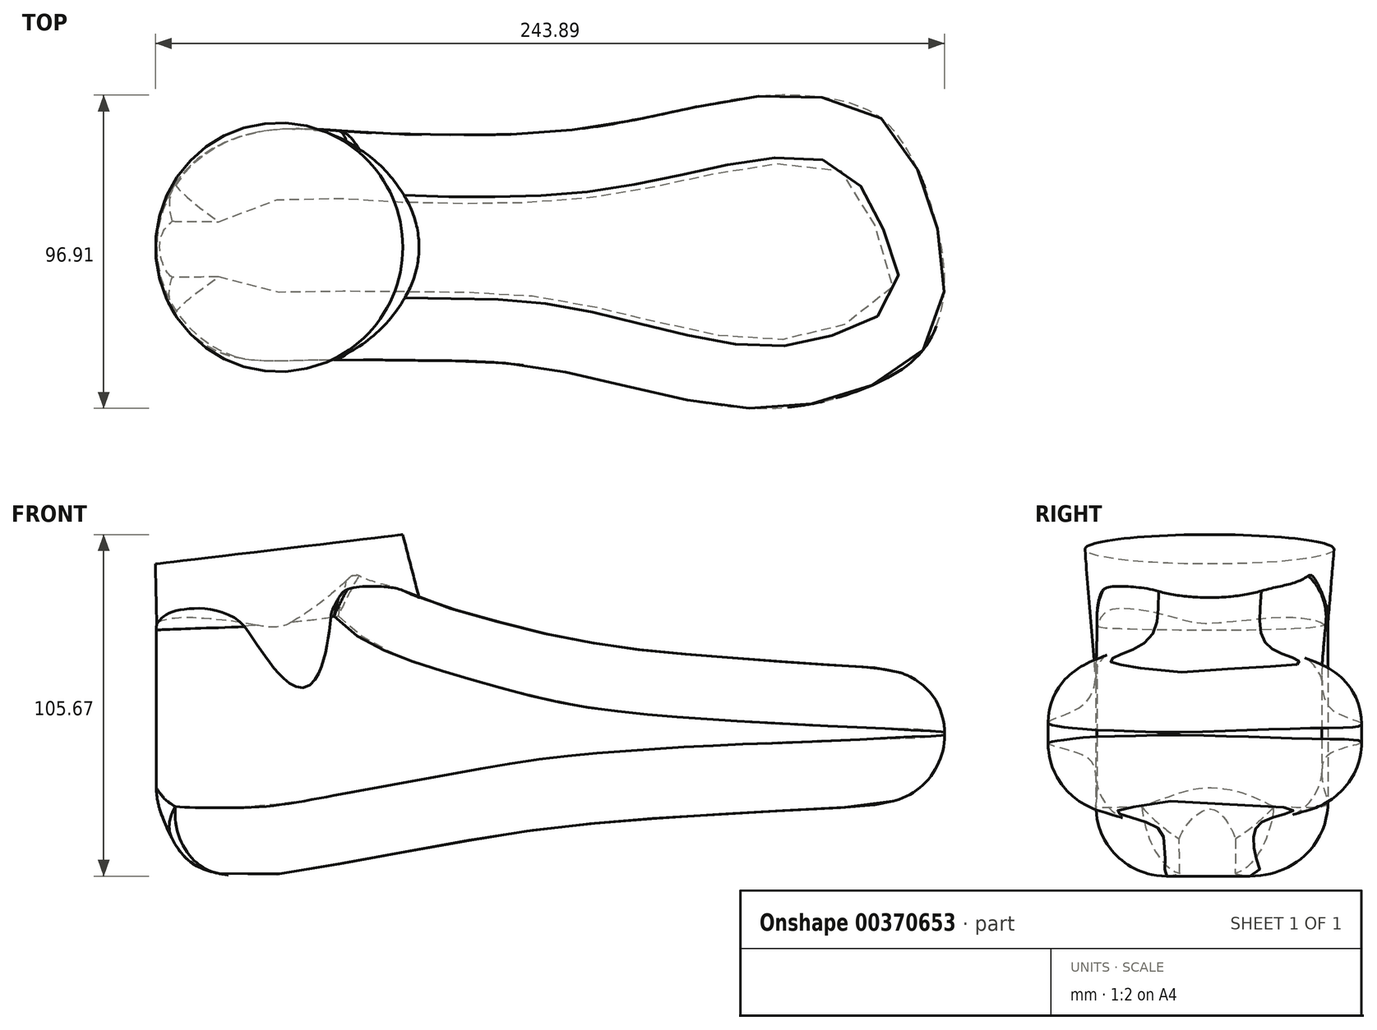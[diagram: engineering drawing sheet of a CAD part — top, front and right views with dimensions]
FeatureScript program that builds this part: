
annotation { "Feature Type Name" : "Feature", "Feature Type Description" : "" }
export const myFeature = defineFeature(function(context is Context, id is Id, definition is map)
    precondition{}
    {
        {
            var Q0;
            Q0=qCreatedBy(makeId("Top.planeOp"),FACE);
            cPlane(context, id + "F0", {"entities" : qUnion([Q0]), "cplaneType" : CPlaneType.OFFSET, "offset" : 10 * mm, "oppositeDirection" : true, "width" : 150 * mm, "height" : 150 * mm});
        }
        {
            var Q0;
            Q0=qCreatedBy(makeId("Front.planeOp"),FACE);
            var sketch = newSketch(context, id + "F1", { "sketchPlane" : qUnion([Q0])});
            skLineSegment(sketch, "E0", {"start": v(-126.2, 34.59) * mm, "end": v(0, 49.64) * mm, "construction": true});
            skSolve(sketch);
        }
        {
            var Q0;
            Q0=qCreatedBy(makeId("Right.planeOp"),FACE);
            var sketch = newSketch(context, id + "F2", { "sketchPlane" : qUnion([Q0])});
            skLineSegment(sketch, "E1.0", {"start": v(0, 34.59) * mm, "end": v(0, 49.64) * mm, "construction": true});
            skLineSegment(sketch, "E2", {"start": v(0, 49.64) * mm, "end": v(78.18, 49.64) * mm, "construction": true});
            skSolve(sketch);
        }
        {
            var Q0;
            Q0=sQuery(id+"F2.wireOp",VERTEX,"E2.end");
            var Q1;
            Q1=sQuery(id+"F2.wireOp",VERTEX,"E2.start");
            var Q2;
            Q2=sQuery(id+"F1.wireOp",VERTEX,"E0.start");
            cPlane(context, id + "F3", {"entities" : qUnion([Q0, Q1, Q2]), "cplaneType" : CPlaneType.THREE_POINT, "offset" : 25 * mm, "width" : 150 * mm, "height" : 150 * mm});
        }
        {
            var Q0;
            Q0=qCreatedBy(id+"F0.planeOp",FACE);
            cPlane(context, id + "F4", {"entities" : qUnion([Q0]), "cplaneType" : CPlaneType.OFFSET, "offset" : 70 * mm, "width" : 150 * mm, "height" : 150 * mm});
        }
        {
            var Q0;
            Q0=qCreatedBy(id+"F4.planeOp",FACE);
            var sketch = newSketch(context, id + "F5", { "sketchPlane" : qUnion([Q0])});
            skLineSegment(sketch, "E3.bottom", {"start": v(178, 87.04) * mm, "end": v(-168.77, 87.04) * mm});
            skLineSegment(sketch, "E3.top", {"start": v(178, -71.84) * mm, "end": v(-168.77, -71.84) * mm});
            skLineSegment(sketch, "E3.left", {"start": v(178, 87.04) * mm, "end": v(178, -71.84) * mm});
            skLineSegment(sketch, "E3.right", {"start": v(-168.77, 87.04) * mm, "end": v(-168.77, -71.84) * mm});
            skFitSpline(sketch, "E4", {"points": [v(112.25, -42.37) * mm, v(125.46, -31.4) * mm, v(130.92, -15.26) * mm, v(129.4, 3.7) * mm, v(122.2, 25.52) * mm, v(108.35, 43.13) * mm, v(82.74, 48.96) * mm, v(59.98, 47) * mm, v(19.69, 38.96) * mm, v(-18.8, 36.21) * mm, v(-55.07, 36.97) * mm, v(-78, 38.15) * mm, v(-97.37, 35.08) * mm, v(-113.72, 24.15) * mm, v(-122.11, 6.16) * mm, v(-120.89, -12.02) * mm, v(-115.3, -23.54) * mm, v(-105.57, -32.28) * mm, v(-91.66, -36.26) * mm, v(-71.4, -36.26) * mm, v(-39.4, -36.46) * mm, v(-2.44, -38.24) * mm, v(40.03, -47.42) * mm, v(79.93, -51.64) * mm, v(112.25, -42.37) * mm]});
            skSolve(sketch);
        }
        {
            var Q0;
            Q0=qCreatedBy(makeId("Front.planeOp"),FACE);
            var sketch = newSketch(context, id + "F6", { "sketchPlane" : qUnion([Q0])});
            skFitSpline(sketch, "E5", {"points": [v(-119.13, 38.44) * mm, v(-119.13, 33.94) * mm, v(-120.9, 4.27) * mm, v(-123.57, -25.48) * mm, v(-120.92, -39.45) * mm, v(-113.66, -52.87) * mm, v(-104.36, -58.06) * mm, v(-92.75, -59.32) * mm, v(-77.53, -57.75) * mm, v(-27.63, -48.8) * mm, v(12.86, -42.84) * mm, v(69.82, -38.75) * mm, v(100.89, -37.03) * mm, v(116.9, -34.52) * mm, v(127.68, -28.43) * mm, v(131.34, -21.72) * mm, v(132.41, -11.5) * mm, v(130.12, -3.1) * mm, v(121.42, 4.53) * mm, v(108.1, 7.85) * mm, v(96.18, 8.64) * mm, v(56.48, 11.46) * mm, v(17.18, 15.9) * mm, v(-17.61, 23.97) * mm, v(-45.56, 34.04) * mm, v(-53.77, 42.25) * mm, v(-55.62, 46.48) * mm, v(-60.65, 45.69) * mm, v(-113.57, 39.24) * mm, v(-119.13, 38.44) * mm]});
            skSolve(sketch);
        }
        {
            var Q0;
            Q0 = qSketchRegion(id + "F6", true);
            extrude(context, id + "F7", {"entities" : qUnion([Q0]), "depth" : 140 * mm, "symmetric" : true});
        }
        {
            var Q0;
            Q0=makeQuery(id+"F5.imprint","IMPRINT",FACE,{"disambiguationData":[TD([[makeQuery(id+"F5.imprint","IMPRINT",EDGE,{"derivedFrom":sQuery(id+"F5.wireOp",EDGE,"E3.bottom")}),1.0]])]});
            extrude(context, id + "F8", {"entities" : qUnion([Q0]), "operationType" : NewBodyOperationType.REMOVE, "oppositeDirection" : true, "depth" : 130 * mm});
        }
        {
            var Q0;
            Q0=makeQuery(id+"F8.boolean.opBoolean","INTERSECT",EDGE,{"disambiguationData":[OD(1.0)],"derivedFrom":[makeQuery(id+"F7.opExtrude","SWEPT_FACE",FACE,{"disambiguationData":[OSD([sQuery(id+"F6.wireOp",EDGE,"E5")])]}),makeQuery(id+"F8.opExtrude","SWEPT_FACE",FACE,{"disambiguationData":[OSD([sQuery(id+"F5.wireOp",EDGE,"E4")])]})]});
            fillet(context, id + "F9", {"entities" : qUnion([Q0]), "radius" : 20 * mm, "allowEdgeOverflow" : false});
        }
        {
            var Q0;
            Q0=makeQuery(id+"F8.boolean.opBoolean","INTERSECT",EDGE,{"disambiguationData":[OD(0.0)],"derivedFrom":[makeQuery(id+"F7.opExtrude","SWEPT_FACE",FACE,{"disambiguationData":[OSD([sQuery(id+"F6.wireOp",EDGE,"E5")])]}),makeQuery(id+"F8.opExtrude","SWEPT_FACE",FACE,{"disambiguationData":[OSD([sQuery(id+"F5.wireOp",EDGE,"E4")])]})]});
            fillet(context, id + "F10", {"entities" : qUnion([Q0]), "radius" : 22 * mm, "tangentPropagation" : true, "allowEdgeOverflow" : false});
        }
        {
            var Q0;
            Q0=qCreatedBy(id+"F3.planeOp",FACE);
            var sketch = newSketch(context, id + "F11", { "sketchPlane" : qUnion([Q0])});
            skLineSegment(sketch, "E6.bottom", {"start": v(-167.37, -58.49) * mm, "end": v(31.87, -58.49) * mm});
            skLineSegment(sketch, "E6.top", {"start": v(-167.37, 81.96) * mm, "end": v(31.87, 81.96) * mm});
            skLineSegment(sketch, "E6.left", {"start": v(-167.37, -58.49) * mm, "end": v(-167.37, 81.96) * mm});
            skLineSegment(sketch, "E6.right", {"start": v(31.87, -58.49) * mm, "end": v(31.87, 81.96) * mm});
            skSolve(sketch);
        }
        {
            var Q0;
            Q0=makeQuery(id+"F11.imprint","IMPRINT",FACE,{"disambiguationData":[TD([[makeQuery(id+"F11.imprint","IMPRINT",EDGE,{"derivedFrom":sQuery(id+"F11.wireOp",EDGE,"E6.bottom")}),1.0]])]});
            extrude(context, id + "F12", {"entities" : qUnion([Q0]), "operationType" : NewBodyOperationType.REMOVE, "depth" : 10 * mm, "symmetric" : true});
        }
        {
            var Q0;
            Q0=makeQuery(id+"F7.opExtrude","SWEPT_BODY",BODY,{"disambiguationData":[OSD([sQuery(id+"F6.wireOp",EDGE,"E5")])]});
            var Q1;
            Q1=qCreatedBy(makeId("Origin.pointOp"),VERTEX);
            transform(context, id + "F13", {"entities" : qUnion([Q0]), "transformType" : TransformType.SCALE_UNIFORMLY, "scale" : 0.96, "scalePoint" : qUnion([Q1]), "makeCopy" : false});
        }
        {
            var Q0;
            Q0=qCreatedBy(id+"F3.planeOp",FACE);
            cPlane(context, id + "F14", {"entities" : qUnion([Q0]), "cplaneType" : CPlaneType.OFFSET, "offset" : 96 * mm, "oppositeDirection" : true, "width" : 150 * mm, "height" : 150 * mm});
        }
        {
            var Q0;
            Q0=qCreatedBy(id+"F14.planeOp",FACE);
            cPlane(context, id + "F15", {"entities" : qUnion([Q0]), "cplaneType" : CPlaneType.OFFSET, "offset" : 100 * mm, "width" : 150 * mm, "height" : 150 * mm});
        }
        {
            var Q0;
            Q0=qCreatedBy(id+"F15.planeOp",FACE);
            var sketch = newSketch(context, id + "F16", { "sketchPlane" : qUnion([Q0])});
            skCircle(sketch, "E7", {"center": v(-73.97, 0) * mm, "radius": 38.5 * mm});
            skSolve(sketch);
        }
        {
            var Q0;
            Q0=qCreatedBy(id+"F3.planeOp",FACE);
            cPlane(context, id + "F17", {"entities" : qUnion([Q0]), "cplaneType" : CPlaneType.OFFSET, "offset" : 45 * mm, "oppositeDirection" : true, "width" : 150 * mm, "height" : 150 * mm});
        }
        {
            var Q0;
            Q0=qCreatedBy(id+"F17.planeOp",FACE);
            var sketch = newSketch(context, id + "F18", { "sketchPlane" : qUnion([Q0])});
            skEllipse(sketch, "E8", {"center": v(-73.07, 0) * mm, "majorRadius": 44.16 * mm, "minorRadius": 34.46 * mm, "majorAxis": v(1, 0)});
            skSolve(sketch);
        }
        {
            var Q1;
            Q1 = qSketchRegion(id + "F16", true);
            var Q2;
            Q2 = qSketchRegion(id + "F18", true);
            loft(context, id + "F19", {"operationType" : NewBodyOperationType.ADD, "sheetProfilesArray" : [{ "sheetProfileEntities" : qUnion([Q1]) }, { "sheetProfileEntities" : qUnion([Q2]) }]});
        }
    });
